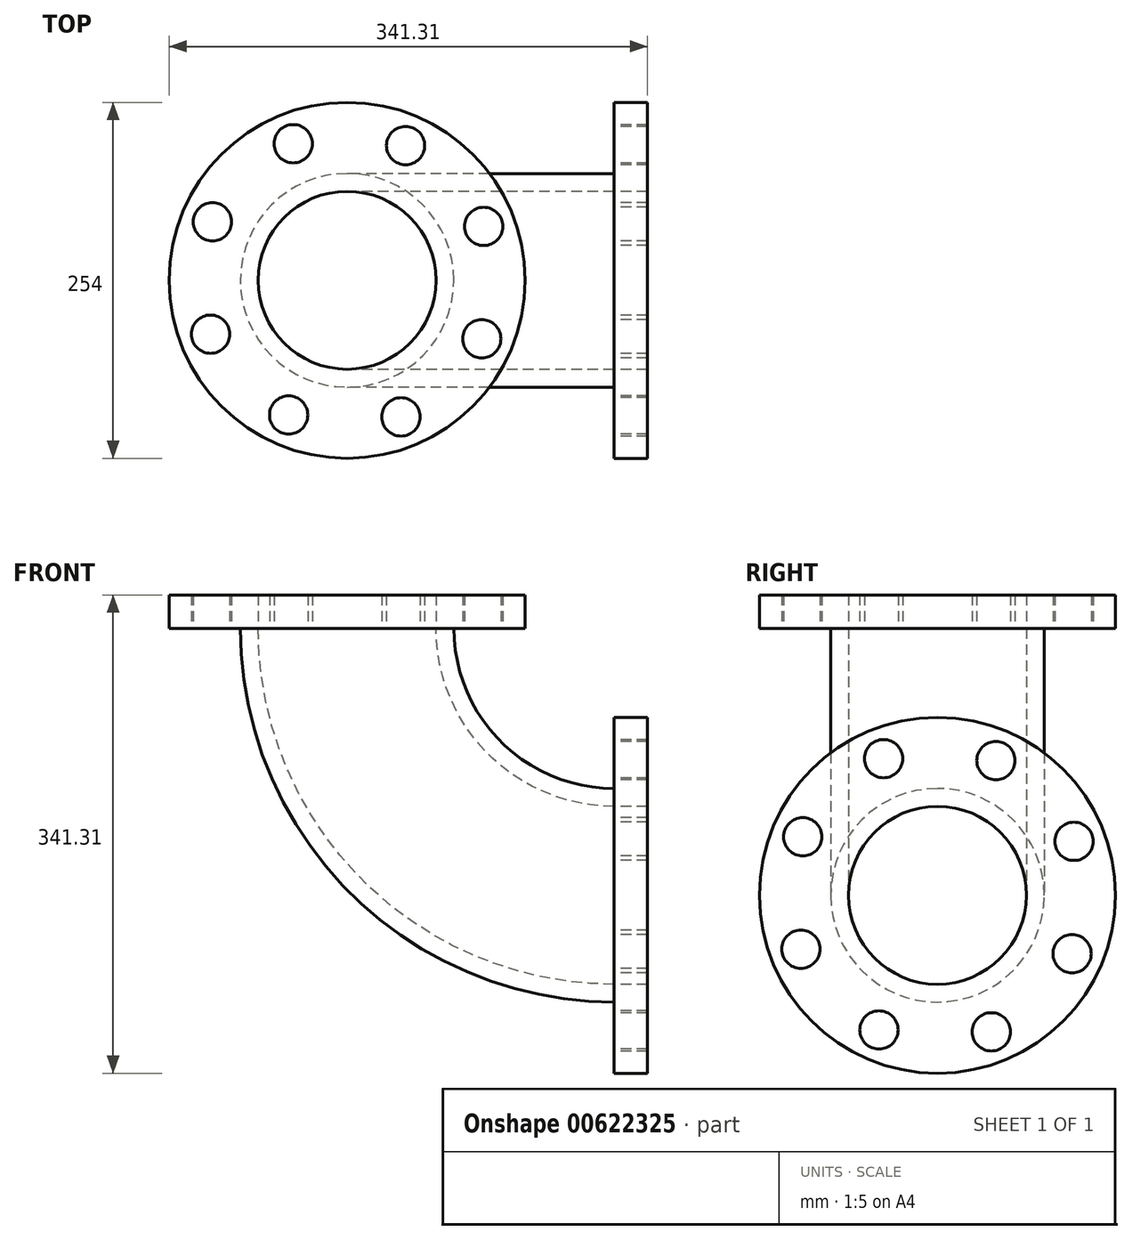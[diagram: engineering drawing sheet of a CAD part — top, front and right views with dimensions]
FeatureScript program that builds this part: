
annotation { "Feature Type Name" : "Feature", "Feature Type Description" : "" }
export const myFeature = defineFeature(function(context is Context, id is Id, definition is map)
    precondition{}
    {
        {
            var Q0;
            Q0=qCreatedBy(makeId("Top.planeOp"),FACE);
            var sketch = newSketch(context, id + "F0", { "sketchPlane" : qUnion([Q0])});
            skCircle(sketch, "E0", {"center": v(0, 0) * mm, "radius": 63.5 * mm});
            skCircle(sketch, "E1", {"center": v(0, 0) * mm, "radius": 127 * mm});
            skCircle(sketch, "E2", {"center": v(41.72, 96.11) * mm, "radius": 13.66 * mm});
            skCircle(sketch, "E3", {"center": v(97.46, 38.46) * mm, "radius": 13.66 * mm});
            skCircle(sketch, "E4", {"center": v(96.11, -41.72) * mm, "radius": 13.66 * mm});
            skCircle(sketch, "E5", {"center": v(38.46, -97.46) * mm, "radius": 13.66 * mm});
            skCircle(sketch, "E6", {"center": v(-41.72, -96.11) * mm, "radius": 13.66 * mm});
            skCircle(sketch, "E7", {"center": v(-97.46, -38.46) * mm, "radius": 13.66 * mm});
            skCircle(sketch, "E8", {"center": v(-96.11, 41.72) * mm, "radius": 13.66 * mm});
            skCircle(sketch, "E9", {"center": v(-38.46, 97.46) * mm, "radius": 13.66 * mm});
            skCircle(sketch, "E10", {"center": v(0, 0) * mm, "radius": 104.78 * mm});
            skCircle(sketch, "E11", {"center": v(0, 0) * mm, "radius": 76.2 * mm});
            skLineSegment(sketch, "E12", {"start": v(190.5, -123.52) * mm, "end": v(190.5, 87.54) * mm, "construction": true});
            skSolve(sketch);
        }
        {
            var Q0;
            Q0=makeQuery(id+"F0.imprint","IMPRINT",FACE,{"disambiguationData":[TD([[makeQuery(id+"F0.imprint","IMPRINT",EDGE,{"derivedFrom":sQuery(id+"F0.wireOp",EDGE,"E1")}),1.0]])]});
            var Q1;
            Q1=makeQuery(id+"F0.imprint","IMPRINT",FACE,{"disambiguationData":[TD([[makeQuery(id+"F0.imprint","IMPRINT",EDGE,{"derivedFrom":sQuery(id+"F0.wireOp",EDGE,"E0")}),-1.0]])]});
            var Q2;
            Q2=makeQuery(id+"F0.imprint","IMPRINT",FACE,{"disambiguationData":[TD([[makeQuery(id+"F0.imprint","IMPRINT",EDGE,{"derivedFrom":sQuery(id+"F0.wireOp",EDGE,"E11")}),-1.0]])]});
            extrude(context, id + "F1", {"entities" : qUnion([Q0, Q1, Q2]), "depth" : 23.8 * mm, "offsetDistance" : 25.4 * mm});
        }
        {
            var Q0;
            Q0=makeQuery(id+"F0.imprint","IMPRINT",FACE,{"disambiguationData":[TD([[makeQuery(id+"F0.imprint","IMPRINT",EDGE,{"derivedFrom":sQuery(id+"F0.wireOp",EDGE,"E0")}),-1.0]])]});
            var Q1;
            Q1=sQuery(id+"F0.wireOp",EDGE,"E12");
            revolve(context, id + "F2", {"operationType" : NewBodyOperationType.ADD, "entities" : qUnion([Q0]), "axis" : qUnion([Q1]), "revolveType" : RevolveType.ONE_DIRECTION, "oppositeDirection" : true, "angle" : 90 * degree});
        }
        {
            var Q0;
            Q0=makeQuery(id+"F2.opRevolve","CAP_FACE",FACE,{"disambiguationData":[OSD([sQuery(id+"F0.wireOp",EDGE,"E0"),sQuery(id+"F0.wireOp",EDGE,"E11")])],"isStart":false});
            var sketch = newSketch(context, id + "F3", { "sketchPlane" : qUnion([Q0])});
            skCircle(sketch, "E13", {"center": v(0, -190.5) * mm, "radius": 63.5 * mm});
            skCircle(sketch, "E14", {"center": v(0, -190.5) * mm, "radius": 127 * mm});
            skCircle(sketch, "E15", {"center": v(41.72, -94.39) * mm, "radius": 13.66 * mm});
            skCircle(sketch, "E16", {"center": v(97.46, -152.04) * mm, "radius": 13.66 * mm});
            skCircle(sketch, "E17", {"center": v(96.11, -232.22) * mm, "radius": 13.66 * mm});
            skCircle(sketch, "E18", {"center": v(38.46, -287.96) * mm, "radius": 13.66 * mm});
            skCircle(sketch, "E19", {"center": v(-41.72, -286.61) * mm, "radius": 13.66 * mm});
            skCircle(sketch, "E20", {"center": v(-97.46, -228.96) * mm, "radius": 13.66 * mm});
            skCircle(sketch, "E21", {"center": v(-96.11, -148.78) * mm, "radius": 13.66 * mm});
            skCircle(sketch, "E22", {"center": v(-38.46, -93.04) * mm, "radius": 13.66 * mm});
            skCircle(sketch, "E23", {"center": v(0, -190.5) * mm, "radius": 104.78 * mm});
            skCircle(sketch, "E24", {"center": v(0, -190.5) * mm, "radius": 76.2 * mm});
            skSolve(sketch);
        }
        {
            var Q0;
            Q0=makeQuery(id+"F3.imprint","IMPRINT",FACE,{"disambiguationData":[TD([[makeQuery(id+"F3.imprint","IMPRINT",EDGE,{"derivedFrom":sQuery(id+"F3.wireOp",EDGE,"E24")}),1.0]])]});
            var Q1;
            Q1=makeQuery(id+"F3.imprint","IMPRINT",FACE,{"disambiguationData":[TD([[makeQuery(id+"F3.imprint","IMPRINT",EDGE,{"derivedFrom":sQuery(id+"F3.wireOp",EDGE,"E14")}),1.0]])]});
            var Q2;
            Q2=makeQuery(id+"F3.imprint","IMPRINT",FACE,{"disambiguationData":[TD([[makeQuery(id+"F3.imprint","IMPRINT",EDGE,{"derivedFrom":sQuery(id+"F3.wireOp",EDGE,"E13")}),1.0]])]});
            extrude(context, id + "F4", {"entities" : qUnion([Q0, Q1, Q2]), "operationType" : NewBodyOperationType.ADD, "depth" : 23.8 * mm, "offsetDistance" : 25.4 * mm});
        }
    });
